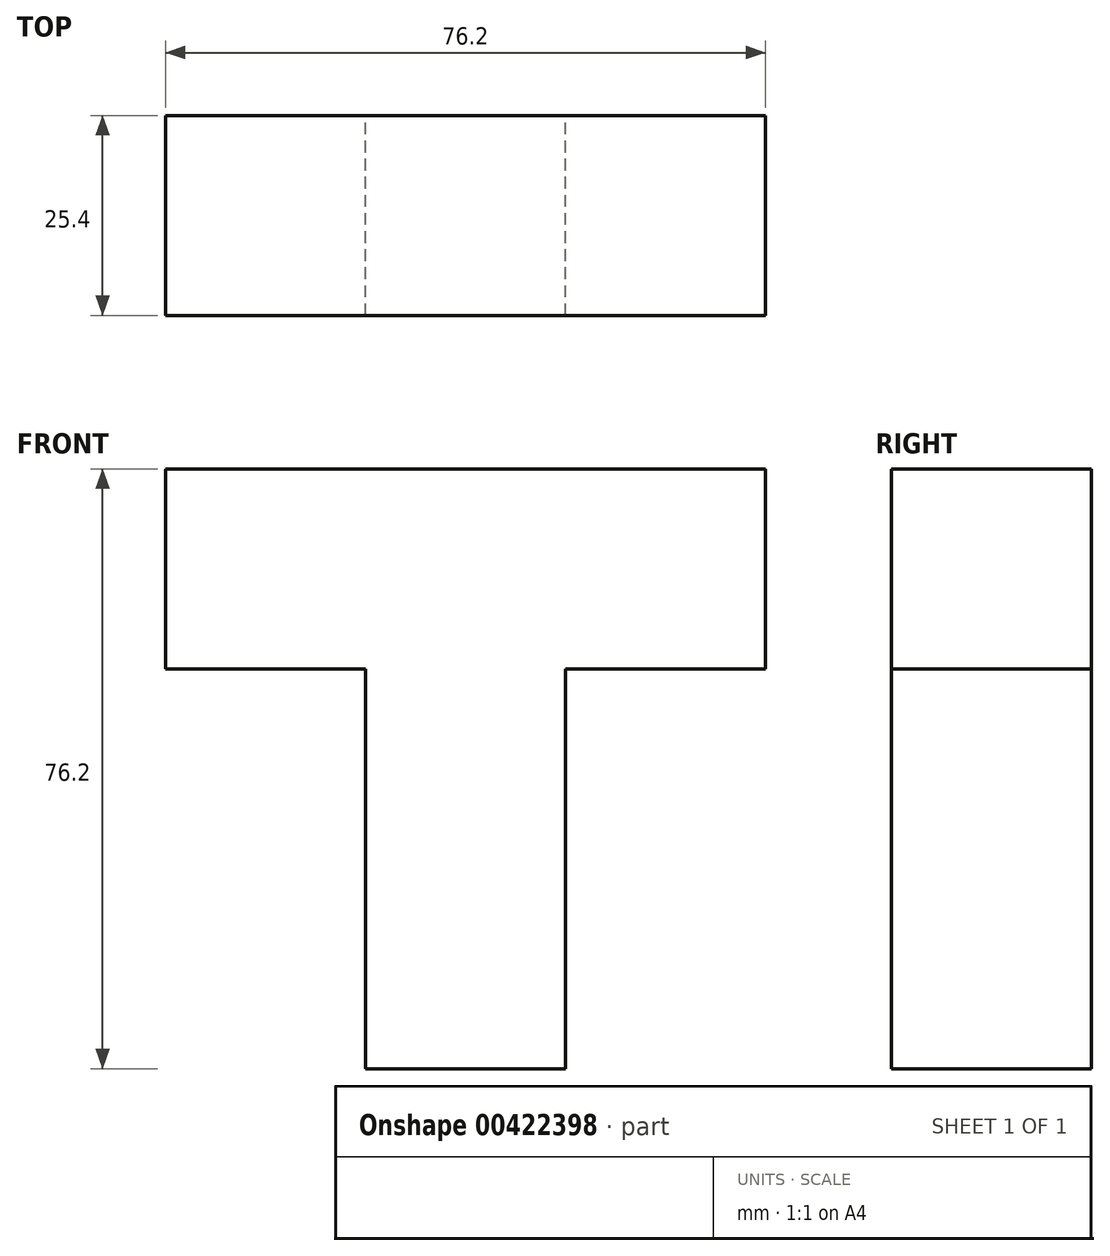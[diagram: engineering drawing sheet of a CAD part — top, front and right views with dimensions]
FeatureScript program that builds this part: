
annotation { "Feature Type Name" : "Feature", "Feature Type Description" : "" }
export const myFeature = defineFeature(function(context is Context, id is Id, definition is map)
    precondition{}
    {
        {
            var Q0;
            Q0=qCreatedBy(makeId("Front.planeOp"),FACE);
            var sketch = newSketch(context, id + "F0", { "sketchPlane" : qUnion([Q0])});
            skLineSegment(sketch, "E0", {"start": v(-42.96, 0) * mm, "end": v(33.24, 0) * mm});
            skLineSegment(sketch, "E1", {"start": v(33.24, 0) * mm, "end": v(33.24, -25.4) * mm});
            skLineSegment(sketch, "E2", {"start": v(33.24, -25.4) * mm, "end": v(7.84, -25.4) * mm});
            skLineSegment(sketch, "E3", {"start": v(7.84, -25.4) * mm, "end": v(7.84, -76.2) * mm});
            skLineSegment(sketch, "E4", {"start": v(7.84, -76.2) * mm, "end": v(-17.56, -76.2) * mm});
            skLineSegment(sketch, "E5", {"start": v(-17.56, -76.2) * mm, "end": v(-17.56, -25.4) * mm});
            skLineSegment(sketch, "E6", {"start": v(-17.56, -25.4) * mm, "end": v(-42.96, -25.4) * mm});
            skLineSegment(sketch, "E7", {"start": v(-42.96, -25.4) * mm, "end": v(-42.96, 0) * mm});
            skSolve(sketch);
        }
        {
            var Q0;
            Q0 = qSketchRegion(id + "F0", true);
            extrude(context, id + "F1", {"entities" : qUnion([Q0]), "depth" : 25.4 * mm});
        }
    });
